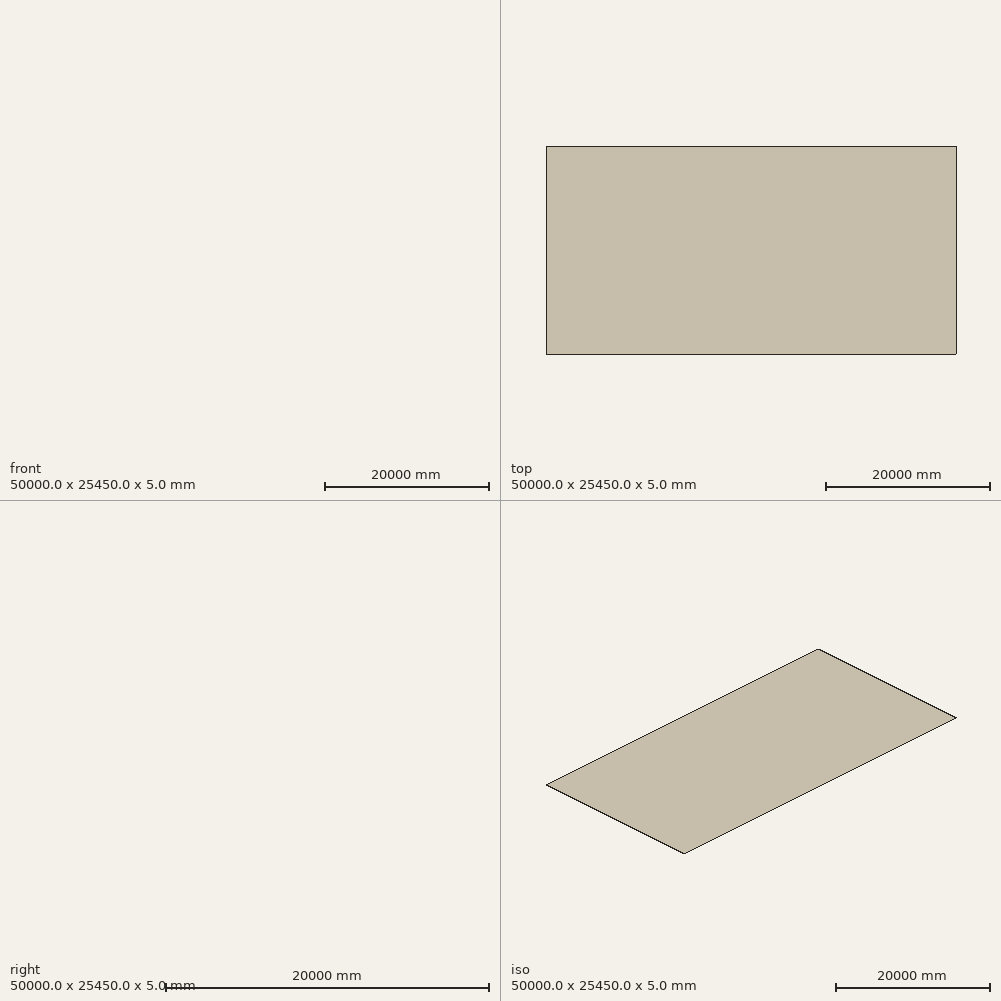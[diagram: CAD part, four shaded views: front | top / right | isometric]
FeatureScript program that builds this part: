
annotation { "Feature Type Name" : "Feature", "Feature Type Description" : "" }
export const myFeature = defineFeature(function(context is Context, id is Id, definition is map)
    precondition{}
    {
        {
            var Q0;
            Q0=qCreatedBy(makeId("Top.planeOp"),FACE);
            var sketch = newSketch(context, id + "F0", { "sketchPlane" : qUnion([Q0])});
            skLineSegment(sketch, "E0.bottom", {"start": v(0, 0) * mm, "end": v(50000, 0) * mm});
            skLineSegment(sketch, "E0.top", {"start": v(0, 25450) * mm, "end": v(50000, 25450) * mm});
            skLineSegment(sketch, "E0.left", {"start": v(0, 0) * mm, "end": v(0, 25450) * mm});
            skLineSegment(sketch, "E0.right", {"start": v(50000, 0) * mm, "end": v(50000, 25450) * mm});
            skSolve(sketch);
        }
        {
            var Q0;
            Q0=makeQuery(id+"F0.imprint","IMPRINT",FACE,{"disambiguationData":[TD([[makeQuery(id+"F0.imprint","IMPRINT",EDGE,{"derivedFrom":sQuery(id+"F0.wireOp",EDGE,"E0.bottom")}),1.0]])]});
            extrude(context, id + "F1", {"entities" : qUnion([Q0]), "depth" : 5 * mm});
        }
    });
